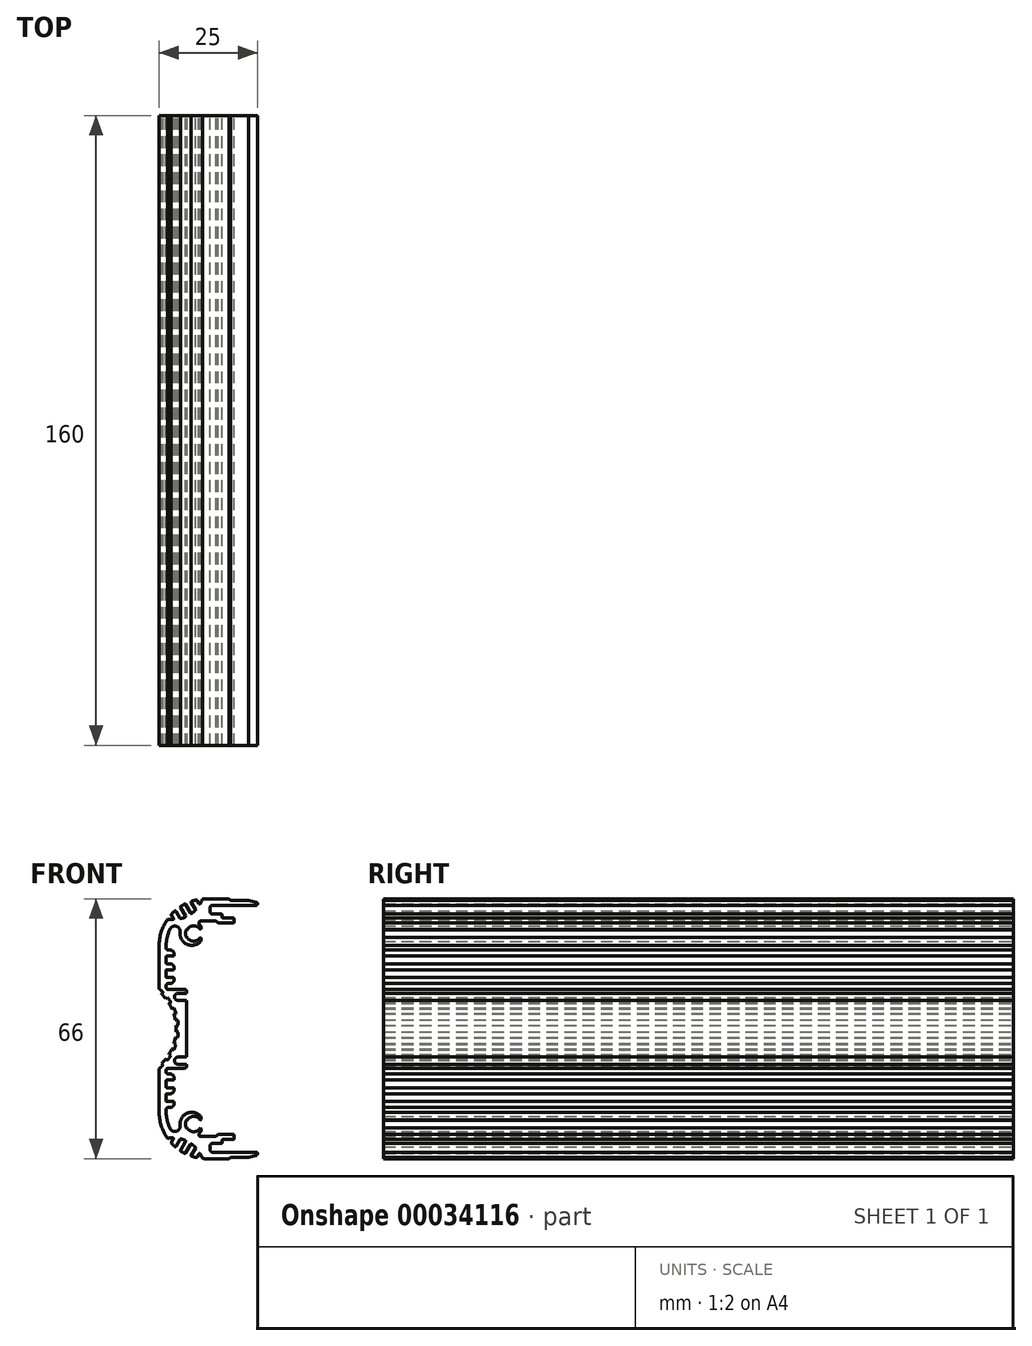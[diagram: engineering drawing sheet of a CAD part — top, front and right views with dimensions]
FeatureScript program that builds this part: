
annotation { "Feature Type Name" : "Feature", "Feature Type Description" : "" }
export const myFeature = defineFeature(function(context is Context, id is Id, definition is map)
    precondition{}
    {
        {
            var Q0;
            Q0=qCreatedBy(makeId("Front.planeOp"),FACE);
            var sketch = newSketch(context, id + "F0", { "sketchPlane" : qUnion([Q0])});
            skArc(sketch, "E0", {"start": v(-7.7, 9) * mm, "mid": v(-8.6, 8.1) * mm, "end": v(-7.7, 7.2) * mm});
            skLineSegment(sketch, "E1", {"start": v(-7.7, 9) * mm, "end": v(-5.5, 9) * mm});
            skLineSegment(sketch, "E2", {"start": v(-5.5, 9) * mm, "end": v(-5.5, 9.5) * mm});
            skArc(sketch, "E3", {"start": v(-5.5, 9.5) * mm, "mid": v(-5.65, 9.85) * mm, "end": v(-6, 10) * mm});
            skLineSegment(sketch, "E4", {"start": v(-6, 10) * mm, "end": v(-10.2, 10) * mm});
            skArc(sketch, "E5", {"start": v(-10.7, 10.5) * mm, "mid": v(-10.55, 10.15) * mm, "end": v(-10.2, 10) * mm});
            skLineSegment(sketch, "E6", {"start": v(-10.7, 10.5) * mm, "end": v(-10.7, 11) * mm});
            skArc(sketch, "E7", {"start": v(-10.2, 11.5) * mm, "mid": v(-10.55, 11.35) * mm, "end": v(-10.7, 11) * mm});
            skLineSegment(sketch, "E8", {"start": v(-10.2, 11.5) * mm, "end": v(-9.7, 11.5) * mm});
            skArc(sketch, "E9", {"start": v(-9.7, 11.5) * mm, "mid": v(-9, 11.8) * mm, "end": v(-8.7, 12.5) * mm});
            skLineSegment(sketch, "E10", {"start": v(-8.7, 12.5) * mm, "end": v(-8.7, 12.8) * mm});
            skArc(sketch, "E11", {"start": v(-8.7, 12.8) * mm, "mid": v(-8.76, 12.94) * mm, "end": v(-8.9, 13) * mm});
            skLineSegment(sketch, "E12", {"start": v(-8.9, 13) * mm, "end": v(-10.5, 13) * mm});
            skArc(sketch, "E13", {"start": v(-10.7, 13.2) * mm, "mid": v(-10.64, 13.06) * mm, "end": v(-10.5, 13) * mm});
            skLineSegment(sketch, "E14", {"start": v(-10.7, 13.2) * mm, "end": v(-10.7, 14.8) * mm});
            skArc(sketch, "E15", {"start": v(-10.5, 15) * mm, "mid": v(-10.64, 14.94) * mm, "end": v(-10.7, 14.8) * mm});
            skLineSegment(sketch, "E16", {"start": v(-10.5, 15) * mm, "end": v(-8.9, 15) * mm});
            skArc(sketch, "E17", {"start": v(-8.9, 15) * mm, "mid": v(-8.76, 15.06) * mm, "end": v(-8.7, 15.2) * mm});
            skLineSegment(sketch, "E18", {"start": v(-8.7, 15.2) * mm, "end": v(-8.7, 15.5) * mm});
            skArc(sketch, "E19", {"start": v(-8.7, 15.5) * mm, "mid": v(-9, 16.2) * mm, "end": v(-9.7, 16.5) * mm});
            skLineSegment(sketch, "E20", {"start": v(-9.7, 16.5) * mm, "end": v(-10.5, 16.5) * mm});
            skArc(sketch, "E21", {"start": v(-10.7, 16.7) * mm, "mid": v(-10.64, 16.56) * mm, "end": v(-10.5, 16.5) * mm});
            skLineSegment(sketch, "E22", {"start": v(-10.7, 16.7) * mm, "end": v(-10.7, 18.3) * mm});
            skArc(sketch, "E23", {"start": v(-10.5, 18.5) * mm, "mid": v(-10.64, 18.44) * mm, "end": v(-10.7, 18.3) * mm});
            skLineSegment(sketch, "E24", {"start": v(-10.5, 18.5) * mm, "end": v(-8.9, 18.5) * mm});
            skArc(sketch, "E25", {"start": v(-8.9, 18.5) * mm, "mid": v(-8.76, 18.56) * mm, "end": v(-8.7, 18.7) * mm});
            skLineSegment(sketch, "E26", {"start": v(-8.7, 18.7) * mm, "end": v(-8.7, 19) * mm});
            skArc(sketch, "E27", {"start": v(-8.7, 19) * mm, "mid": v(-9, 19.7) * mm, "end": v(-9.7, 20) * mm});
            skLineSegment(sketch, "E28", {"start": v(-9.7, 20) * mm, "end": v(-10.2, 20) * mm});
            skArc(sketch, "E29", {"start": v(-10.7, 20.5) * mm, "mid": v(-10.55, 20.15) * mm, "end": v(-10.2, 20) * mm});
            skLineSegment(sketch, "E30", {"start": v(-10.7, 20.5) * mm, "end": v(-10.7, 21) * mm});
            skArc(sketch, "E31", {"start": v(-9.74, 25.33) * mm, "mid": v(-10.46, 23.22) * mm, "end": v(-10.7, 21) * mm});
            skArc(sketch, "E32", {"start": v(-7.18, 24.58) * mm, "mid": v(-8.14, 26.05) * mm, "end": v(-9.74, 25.33) * mm});
            skArc(sketch, "E33", {"start": v(-7.18, 24.58) * mm, "mid": v(-5.47, 21.48) * mm, "end": v(-2, 22.16) * mm});
            skArc(sketch, "E34", {"start": v(-2, 22.16) * mm, "mid": v(-1.8, 22.69) * mm, "end": v(-2.02, 23.2) * mm});
            skArc(sketch, "E35", {"start": v(-5.39, 23.23) * mm, "mid": v(-3.71, 22.25) * mm, "end": v(-2.02, 23.2) * mm});
            skLineSegment(sketch, "E36", {"start": v(-5.39, 23.23) * mm, "end": v(-5.52, 23.15) * mm});
            skArc(sketch, "E37", {"start": v(-5.52, 25.25) * mm, "mid": v(-5.8, 24.2) * mm, "end": v(-5.52, 23.15) * mm});
            skLineSegment(sketch, "E38", {"start": v(-5.52, 25.25) * mm, "end": v(-5.39, 25.18) * mm});
            skArc(sketch, "E39", {"start": v(-2.02, 25.2) * mm, "mid": v(-3.71, 26.15) * mm, "end": v(-5.39, 25.17) * mm});
            skArc(sketch, "E40", {"start": v(-2.02, 25.2) * mm, "mid": v(-1.8, 25.71) * mm, "end": v(-2, 26.24) * mm});
            skArc(sketch, "E41", {"start": v(-2, 26.24) * mm, "mid": v(-2.12, 26.36) * mm, "end": v(-2.24, 26.47) * mm});
            skArc(sketch, "E42", {"start": v(-1.91, 27.35) * mm, "mid": v(-2.38, 27.02) * mm, "end": v(-2.24, 26.47) * mm});
            skLineSegment(sketch, "E43", {"start": v(-1.91, 27.35) * mm, "end": v(2, 27.35) * mm});
            skLineSegment(sketch, "E44", {"start": v(2, 27.35) * mm, "end": v(2.5, 26.85) * mm});
            skLineSegment(sketch, "E45", {"start": v(2.5, 26.85) * mm, "end": v(6.3, 26.85) * mm});
            skArc(sketch, "E46", {"start": v(6.3, 26.85) * mm, "mid": v(6.44, 26.9) * mm, "end": v(6.5, 27.05) * mm});
            skLineSegment(sketch, "E47", {"start": v(6.5, 27.05) * mm, "end": v(6.5, 27.95) * mm});
            skArc(sketch, "E48", {"start": v(6.5, 27.95) * mm, "mid": v(6.44, 28.1) * mm, "end": v(6.3, 28.15) * mm});
            skLineSegment(sketch, "E49", {"start": v(6.3, 28.15) * mm, "end": v(3.7, 28.15) * mm});
            skArc(sketch, "E50", {"start": v(3.5, 28.35) * mm, "mid": v(3.56, 28.2) * mm, "end": v(3.7, 28.15) * mm});
            skLineSegment(sketch, "E51", {"start": v(3.5, 28.35) * mm, "end": v(3.5, 28.95) * mm});
            skArc(sketch, "E52", {"start": v(3.5, 28.95) * mm, "mid": v(3.44, 29.1) * mm, "end": v(3.3, 29.15) * mm});
            skLineSegment(sketch, "E53", {"start": v(3.3, 29.15) * mm, "end": v(1, 29.15) * mm});
            skArc(sketch, "E54", {"start": v(0.5, 29.65) * mm, "mid": v(0.65, 29.3) * mm, "end": v(1, 29.15) * mm});
            skLineSegment(sketch, "E55", {"start": v(0.5, 29.65) * mm, "end": v(0.5, 30.85) * mm});
            skArc(sketch, "E56", {"start": v(1, 31.35) * mm, "mid": v(0.65, 31.2) * mm, "end": v(0.5, 30.85) * mm});
            skLineSegment(sketch, "E57", {"start": v(1, 31.35) * mm, "end": v(12.1, 31.35) * mm});
            skArc(sketch, "E58", {"start": v(12.1, 31.35) * mm, "mid": v(12.5, 31.7) * mm, "end": v(12.2, 32.14) * mm});
            skLineSegment(sketch, "E59", {"start": v(12.2, 32.14) * mm, "end": v(10.29, 32.65) * mm});
            skLineSegment(sketch, "E60", {"start": v(10.29, 32.65) * mm, "end": v(5.65, 32.65) * mm});
            skLineSegment(sketch, "E61", {"start": v(5.65, 32.65) * mm, "end": v(5.3, 33) * mm});
            skLineSegment(sketch, "E62", {"start": v(5.3, 33) * mm, "end": v(-0.5, 33) * mm});
            skArc(sketch, "E63", {"start": v(-0.5, 33) * mm, "mid": v(-1, 32.99) * mm, "end": v(-1.5, 32.96) * mm});
            skArc(sketch, "E64", {"start": v(-2.04, 31.77) * mm, "mid": v(-1.74, 32.36) * mm, "end": v(-1.5, 32.96) * mm});
            skArc(sketch, "E65", {"start": v(-2.39, 31.77) * mm, "mid": v(-2.21, 31.67) * mm, "end": v(-2.04, 31.77) * mm});
            skLineSegment(sketch, "E66", {"start": v(-2.39, 31.77) * mm, "end": v(-2.88, 32.62) * mm});
            skArc(sketch, "E67", {"start": v(-2.88, 32.62) * mm, "mid": v(-2.97, 32.7) * mm, "end": v(-3.1, 32.72) * mm});
            skArc(sketch, "E68", {"start": v(-3.1, 32.72) * mm, "mid": v(-3.66, 32.58) * mm, "end": v(-4.21, 32.41) * mm});
            skArc(sketch, "E69", {"start": v(-4.21, 32.41) * mm, "mid": v(-4.34, 32.3) * mm, "end": v(-4.32, 32.12) * mm});
            skLineSegment(sketch, "E70", {"start": v(-4.32, 32.12) * mm, "end": v(-3.29, 30.33) * mm});
            skArc(sketch, "E71", {"start": v(-3.32, 30.09) * mm, "mid": v(-3.26, 30.2) * mm, "end": v(-3.29, 30.33) * mm});
            skArc(sketch, "E72", {"start": v(-4.18, 29.33) * mm, "mid": v(-3.74, 29.7) * mm, "end": v(-3.32, 30.09) * mm});
            skArc(sketch, "E73", {"start": v(-4.48, 29.4) * mm, "mid": v(-4.34, 29.3) * mm, "end": v(-4.18, 29.33) * mm});
            skLineSegment(sketch, "E74", {"start": v(-4.48, 29.4) * mm, "end": v(-5.74, 31.58) * mm});
            skArc(sketch, "E75", {"start": v(-5.74, 31.58) * mm, "mid": v(-5.86, 31.68) * mm, "end": v(-6, 31.66) * mm});
            skArc(sketch, "E76", {"start": v(-6, 31.66) * mm, "mid": v(-6.5, 31.4) * mm, "end": v(-6.98, 31.1) * mm});
            skArc(sketch, "E77", {"start": v(-6.98, 31.1) * mm, "mid": v(-7.07, 30.98) * mm, "end": v(-7.04, 30.83) * mm});
            skLineSegment(sketch, "E78", {"start": v(-7.04, 30.83) * mm, "end": v(-5.78, 28.64) * mm});
            skArc(sketch, "E79", {"start": v(-5.87, 28.36) * mm, "mid": v(-5.76, 28.48) * mm, "end": v(-5.78, 28.64) * mm});
            skArc(sketch, "E80", {"start": v(-6.96, 27.98) * mm, "mid": v(-6.41, 28.15) * mm, "end": v(-5.87, 28.36) * mm});
            skArc(sketch, "E81", {"start": v(-7.19, 28.08) * mm, "mid": v(-7.09, 28) * mm, "end": v(-6.96, 27.98) * mm});
            skLineSegment(sketch, "E82", {"start": v(-7.19, 28.08) * mm, "end": v(-8.22, 29.87) * mm});
            skArc(sketch, "E83", {"start": v(-8.22, 29.87) * mm, "mid": v(-8.36, 29.97) * mm, "end": v(-8.53, 29.92) * mm});
            skArc(sketch, "E84", {"start": v(-8.53, 29.92) * mm, "mid": v(-8.95, 29.52) * mm, "end": v(-9.35, 29.1) * mm});
            skArc(sketch, "E85", {"start": v(-9.35, 29.1) * mm, "mid": v(-9.4, 29) * mm, "end": v(-9.38, 28.87) * mm});
            skLineSegment(sketch, "E86", {"start": v(-9.38, 28.87) * mm, "end": v(-8.88, 28.02) * mm});
            skArc(sketch, "E87", {"start": v(-9.06, 27.72) * mm, "mid": v(-8.89, 27.82) * mm, "end": v(-8.88, 28.02) * mm});
            skArc(sketch, "E88", {"start": v(-10.36, 27.84) * mm, "mid": v(-9.71, 27.75) * mm, "end": v(-9.06, 27.72) * mm});
            skArc(sketch, "E89", {"start": v(-10.36, 27.84) * mm, "mid": v(-11.95, 24.58) * mm, "end": v(-12.5, 21) * mm});
            skLineSegment(sketch, "E90", {"start": v(-12.5, 21) * mm, "end": v(-12.5, 10.13) * mm});
            skArc(sketch, "E91", {"start": v(-11.49, 9.24) * mm, "mid": v(-11.98, 9.7) * mm, "end": v(-12.5, 10.13) * mm});
            skLineSegment(sketch, "E92", {"start": v(-11.49, 9.24) * mm, "end": v(-11.9, 8.83) * mm});
            skArc(sketch, "E93", {"start": v(-10.82, 7.64) * mm, "mid": v(-11.34, 8.25) * mm, "end": v(-11.9, 8.83) * mm});
            skLineSegment(sketch, "E94", {"start": v(-10.82, 7.64) * mm, "end": v(-10.37, 8) * mm});
            skArc(sketch, "E95", {"start": v(-9.52, 6.79) * mm, "mid": v(-9.92, 7.4) * mm, "end": v(-10.37, 8) * mm});
            skLineSegment(sketch, "E96", {"start": v(-9.52, 6.79) * mm, "end": v(-10.01, 6.48) * mm});
            skArc(sketch, "E97", {"start": v(-9.26, 5.07) * mm, "mid": v(-9.61, 5.79) * mm, "end": v(-10.01, 6.48) * mm});
            skLineSegment(sketch, "E98", {"start": v(-9.26, 5.07) * mm, "end": v(-8.73, 5.3) * mm});
            skArc(sketch, "E99", {"start": v(-8.2, 3.93) * mm, "mid": v(-8.45, 4.63) * mm, "end": v(-8.73, 5.3) * mm});
            skLineSegment(sketch, "E100", {"start": v(-8.2, 3.93) * mm, "end": v(-8.76, 3.75) * mm});
            skArc(sketch, "E101", {"start": v(-8.37, 2.2) * mm, "mid": v(-8.54, 2.98) * mm, "end": v(-8.75, 3.75) * mm});
            skLineSegment(sketch, "E102", {"start": v(-8.37, 2.2) * mm, "end": v(-7.8, 2.3) * mm});
            skArc(sketch, "E103", {"start": v(-7.62, 0.84) * mm, "mid": v(-7.69, 1.57) * mm, "end": v(-7.8, 2.3) * mm});
            skLineSegment(sketch, "E104", {"start": v(-7.62, 0.84) * mm, "end": v(-8.2, 0.8) * mm});
            skArc(sketch, "E105", {"start": v(-8.2, -0.8) * mm, "mid": v(-8.17, 0) * mm, "end": v(-8.2, 0.8) * mm});
            skLineSegment(sketch, "E106", {"start": v(-8.2, -0.8) * mm, "end": v(-7.62, -0.84) * mm});
            skArc(sketch, "E107", {"start": v(-7.8, -2.3) * mm, "mid": v(-7.69, -1.57) * mm, "end": v(-7.62, -0.84) * mm});
            skLineSegment(sketch, "E108", {"start": v(-7.8, -2.3) * mm, "end": v(-8.37, -2.2) * mm});
            skArc(sketch, "E109", {"start": v(-8.75, -3.75) * mm, "mid": v(-8.54, -2.98) * mm, "end": v(-8.37, -2.2) * mm});
            skLineSegment(sketch, "E110", {"start": v(-8.76, -3.75) * mm, "end": v(-8.2, -3.93) * mm});
            skArc(sketch, "E111", {"start": v(-8.73, -5.3) * mm, "mid": v(-8.45, -4.63) * mm, "end": v(-8.2, -3.93) * mm});
            skLineSegment(sketch, "E112", {"start": v(-8.73, -5.3) * mm, "end": v(-9.26, -5.07) * mm});
            skArc(sketch, "E113", {"start": v(-10.01, -6.48) * mm, "mid": v(-9.61, -5.79) * mm, "end": v(-9.26, -5.07) * mm});
            skLineSegment(sketch, "E114", {"start": v(-10.01, -6.48) * mm, "end": v(-9.52, -6.79) * mm});
            skArc(sketch, "E115", {"start": v(-10.37, -8) * mm, "mid": v(-9.92, -7.4) * mm, "end": v(-9.52, -6.79) * mm});
            skLineSegment(sketch, "E116", {"start": v(-10.37, -8) * mm, "end": v(-10.82, -7.64) * mm});
            skArc(sketch, "E117", {"start": v(-11.9, -8.83) * mm, "mid": v(-11.34, -8.25) * mm, "end": v(-10.82, -7.64) * mm});
            skLineSegment(sketch, "E118", {"start": v(-11.9, -8.83) * mm, "end": v(-11.49, -9.24) * mm});
            skArc(sketch, "E119", {"start": v(-12.5, -10.13) * mm, "mid": v(-11.98, -9.7) * mm, "end": v(-11.49, -9.24) * mm});
            skLineSegment(sketch, "E120", {"start": v(-12.5, -10.13) * mm, "end": v(-12.5, -21) * mm});
            skArc(sketch, "E121", {"start": v(-12.5, -21) * mm, "mid": v(-11.95, -24.58) * mm, "end": v(-10.36, -27.84) * mm});
            skArc(sketch, "E122", {"start": v(-9.06, -27.72) * mm, "mid": v(-9.71, -27.75) * mm, "end": v(-10.36, -27.84) * mm});
            skArc(sketch, "E123", {"start": v(-8.88, -28.02) * mm, "mid": v(-8.89, -27.82) * mm, "end": v(-9.06, -27.72) * mm});
            skLineSegment(sketch, "E124", {"start": v(-8.88, -28.02) * mm, "end": v(-9.38, -28.87) * mm});
            skArc(sketch, "E125", {"start": v(-9.38, -28.87) * mm, "mid": v(-9.4, -29) * mm, "end": v(-9.35, -29.1) * mm});
            skArc(sketch, "E126", {"start": v(-9.35, -29.1) * mm, "mid": v(-8.95, -29.52) * mm, "end": v(-8.53, -29.92) * mm});
            skArc(sketch, "E127", {"start": v(-8.53, -29.92) * mm, "mid": v(-8.36, -29.97) * mm, "end": v(-8.22, -29.87) * mm});
            skLineSegment(sketch, "E128", {"start": v(-8.22, -29.87) * mm, "end": v(-7.19, -28.08) * mm});
            skArc(sketch, "E129", {"start": v(-6.96, -27.98) * mm, "mid": v(-7.09, -28) * mm, "end": v(-7.19, -28.08) * mm});
            skArc(sketch, "E130", {"start": v(-5.87, -28.36) * mm, "mid": v(-6.41, -28.15) * mm, "end": v(-6.96, -27.98) * mm});
            skArc(sketch, "E131", {"start": v(-5.78, -28.64) * mm, "mid": v(-5.76, -28.48) * mm, "end": v(-5.87, -28.36) * mm});
            skLineSegment(sketch, "E132", {"start": v(-5.78, -28.64) * mm, "end": v(-7.04, -30.83) * mm});
            skArc(sketch, "E133", {"start": v(-7.04, -30.83) * mm, "mid": v(-7.07, -30.98) * mm, "end": v(-6.98, -31.1) * mm});
            skArc(sketch, "E134", {"start": v(-6.98, -31.1) * mm, "mid": v(-6.5, -31.4) * mm, "end": v(-6, -31.66) * mm});
            skArc(sketch, "E135", {"start": v(-6, -31.66) * mm, "mid": v(-5.86, -31.68) * mm, "end": v(-5.74, -31.58) * mm});
            skLineSegment(sketch, "E136", {"start": v(-5.74, -31.58) * mm, "end": v(-4.48, -29.4) * mm});
            skArc(sketch, "E137", {"start": v(-4.18, -29.33) * mm, "mid": v(-4.34, -29.3) * mm, "end": v(-4.48, -29.4) * mm});
            skArc(sketch, "E138", {"start": v(-3.32, -30.09) * mm, "mid": v(-3.74, -29.7) * mm, "end": v(-4.18, -29.33) * mm});
            skArc(sketch, "E139", {"start": v(-3.29, -30.33) * mm, "mid": v(-3.26, -30.2) * mm, "end": v(-3.32, -30.09) * mm});
            skLineSegment(sketch, "E140", {"start": v(-3.29, -30.33) * mm, "end": v(-4.32, -32.12) * mm});
            skArc(sketch, "E141", {"start": v(-4.32, -32.12) * mm, "mid": v(-4.34, -32.3) * mm, "end": v(-4.21, -32.41) * mm});
            skArc(sketch, "E142", {"start": v(-4.21, -32.41) * mm, "mid": v(-3.66, -32.58) * mm, "end": v(-3.1, -32.72) * mm});
            skArc(sketch, "E143", {"start": v(-3.1, -32.72) * mm, "mid": v(-2.97, -32.7) * mm, "end": v(-2.88, -32.62) * mm});
            skLineSegment(sketch, "E144", {"start": v(-2.88, -32.62) * mm, "end": v(-2.39, -31.77) * mm});
            skArc(sketch, "E145", {"start": v(-2.04, -31.77) * mm, "mid": v(-2.21, -31.67) * mm, "end": v(-2.39, -31.77) * mm});
            skArc(sketch, "E146", {"start": v(-1.5, -32.96) * mm, "mid": v(-1.74, -32.36) * mm, "end": v(-2.04, -31.77) * mm});
            skArc(sketch, "E147", {"start": v(-1.5, -32.96) * mm, "mid": v(-1, -32.99) * mm, "end": v(-0.5, -33) * mm});
            skLineSegment(sketch, "E148", {"start": v(-0.5, -33) * mm, "end": v(5.3, -33) * mm});
            skLineSegment(sketch, "E149", {"start": v(5.3, -33) * mm, "end": v(5.65, -32.65) * mm});
            skLineSegment(sketch, "E150", {"start": v(5.65, -32.65) * mm, "end": v(10.29, -32.65) * mm});
            skLineSegment(sketch, "E151", {"start": v(10.29, -32.65) * mm, "end": v(12.2, -32.14) * mm});
            skArc(sketch, "E152", {"start": v(12.2, -32.14) * mm, "mid": v(12.5, -31.7) * mm, "end": v(12.1, -31.35) * mm});
            skLineSegment(sketch, "E153", {"start": v(12.1, -31.35) * mm, "end": v(1, -31.35) * mm});
            skArc(sketch, "E154", {"start": v(0.5, -30.85) * mm, "mid": v(0.65, -31.2) * mm, "end": v(1, -31.35) * mm});
            skLineSegment(sketch, "E155", {"start": v(0.5, -30.85) * mm, "end": v(0.5, -29.65) * mm});
            skArc(sketch, "E156", {"start": v(1, -29.15) * mm, "mid": v(0.65, -29.3) * mm, "end": v(0.5, -29.65) * mm});
            skLineSegment(sketch, "E157", {"start": v(1, -29.15) * mm, "end": v(3.3, -29.15) * mm});
            skArc(sketch, "E158", {"start": v(3.3, -29.15) * mm, "mid": v(3.44, -29.1) * mm, "end": v(3.5, -28.95) * mm});
            skLineSegment(sketch, "E159", {"start": v(3.5, -28.95) * mm, "end": v(3.5, -28.35) * mm});
            skArc(sketch, "E160", {"start": v(3.7, -28.15) * mm, "mid": v(3.56, -28.2) * mm, "end": v(3.5, -28.35) * mm});
            skLineSegment(sketch, "E161", {"start": v(3.7, -28.15) * mm, "end": v(6.3, -28.15) * mm});
            skArc(sketch, "E162", {"start": v(6.3, -28.15) * mm, "mid": v(6.44, -28.1) * mm, "end": v(6.5, -27.95) * mm});
            skLineSegment(sketch, "E163", {"start": v(6.5, -27.95) * mm, "end": v(6.5, -27.05) * mm});
            skArc(sketch, "E164", {"start": v(6.5, -27.05) * mm, "mid": v(6.44, -26.9) * mm, "end": v(6.3, -26.85) * mm});
            skLineSegment(sketch, "E165", {"start": v(6.3, -26.85) * mm, "end": v(2.5, -26.85) * mm});
            skLineSegment(sketch, "E166", {"start": v(2.5, -26.85) * mm, "end": v(2, -27.35) * mm});
            skLineSegment(sketch, "E167", {"start": v(2, -27.35) * mm, "end": v(-1.91, -27.35) * mm});
            skArc(sketch, "E168", {"start": v(-2.24, -26.47) * mm, "mid": v(-2.38, -27.02) * mm, "end": v(-1.91, -27.35) * mm});
            skArc(sketch, "E169", {"start": v(-2.24, -26.47) * mm, "mid": v(-2.12, -26.36) * mm, "end": v(-2, -26.24) * mm});
            skArc(sketch, "E170", {"start": v(-2, -26.24) * mm, "mid": v(-1.8, -25.71) * mm, "end": v(-2.02, -25.2) * mm});
            skArc(sketch, "E171", {"start": v(-5.39, -25.17) * mm, "mid": v(-3.71, -26.15) * mm, "end": v(-2.02, -25.2) * mm});
            skLineSegment(sketch, "E172", {"start": v(-5.39, -25.18) * mm, "end": v(-5.52, -25.25) * mm});
            skArc(sketch, "E173", {"start": v(-5.52, -23.15) * mm, "mid": v(-5.8, -24.2) * mm, "end": v(-5.52, -25.25) * mm});
            skLineSegment(sketch, "E174", {"start": v(-5.52, -23.15) * mm, "end": v(-5.39, -23.23) * mm});
            skArc(sketch, "E175", {"start": v(-2.02, -23.2) * mm, "mid": v(-3.71, -22.25) * mm, "end": v(-5.39, -23.23) * mm});
            skArc(sketch, "E176", {"start": v(-2.02, -23.2) * mm, "mid": v(-1.8, -22.69) * mm, "end": v(-2, -22.16) * mm});
            skArc(sketch, "E177", {"start": v(-2, -22.16) * mm, "mid": v(-5.47, -21.48) * mm, "end": v(-7.18, -24.58) * mm});
            skArc(sketch, "E178", {"start": v(-9.74, -25.33) * mm, "mid": v(-8.14, -26.05) * mm, "end": v(-7.18, -24.58) * mm});
            skArc(sketch, "E179", {"start": v(-10.7, -21) * mm, "mid": v(-10.46, -23.22) * mm, "end": v(-9.74, -25.33) * mm});
            skLineSegment(sketch, "E180", {"start": v(-10.7, -21) * mm, "end": v(-10.7, -20.5) * mm});
            skArc(sketch, "E181", {"start": v(-10.2, -20) * mm, "mid": v(-10.55, -20.15) * mm, "end": v(-10.7, -20.5) * mm});
            skLineSegment(sketch, "E182", {"start": v(-10.2, -20) * mm, "end": v(-9.7, -20) * mm});
            skArc(sketch, "E183", {"start": v(-9.7, -20) * mm, "mid": v(-9, -19.7) * mm, "end": v(-8.7, -19) * mm});
            skLineSegment(sketch, "E184", {"start": v(-8.7, -19) * mm, "end": v(-8.7, -18.7) * mm});
            skArc(sketch, "E185", {"start": v(-8.7, -18.7) * mm, "mid": v(-8.76, -18.56) * mm, "end": v(-8.9, -18.5) * mm});
            skLineSegment(sketch, "E186", {"start": v(-8.9, -18.5) * mm, "end": v(-10.5, -18.5) * mm});
            skArc(sketch, "E187", {"start": v(-10.7, -18.3) * mm, "mid": v(-10.64, -18.44) * mm, "end": v(-10.5, -18.5) * mm});
            skLineSegment(sketch, "E188", {"start": v(-10.7, -18.3) * mm, "end": v(-10.7, -16.7) * mm});
            skArc(sketch, "E189", {"start": v(-10.5, -16.5) * mm, "mid": v(-10.64, -16.56) * mm, "end": v(-10.7, -16.7) * mm});
            skLineSegment(sketch, "E190", {"start": v(-10.5, -16.5) * mm, "end": v(-9.7, -16.5) * mm});
            skArc(sketch, "E191", {"start": v(-9.7, -16.5) * mm, "mid": v(-9, -16.2) * mm, "end": v(-8.7, -15.5) * mm});
            skLineSegment(sketch, "E192", {"start": v(-8.7, -15.5) * mm, "end": v(-8.7, -15.2) * mm});
            skArc(sketch, "E193", {"start": v(-8.7, -15.2) * mm, "mid": v(-8.76, -15.06) * mm, "end": v(-8.9, -15) * mm});
            skLineSegment(sketch, "E194", {"start": v(-8.9, -15) * mm, "end": v(-10.5, -15) * mm});
            skArc(sketch, "E195", {"start": v(-10.7, -14.8) * mm, "mid": v(-10.64, -14.94) * mm, "end": v(-10.5, -15) * mm});
            skLineSegment(sketch, "E196", {"start": v(-10.7, -14.8) * mm, "end": v(-10.7, -13.2) * mm});
            skArc(sketch, "E197", {"start": v(-10.5, -13) * mm, "mid": v(-10.64, -13.06) * mm, "end": v(-10.7, -13.2) * mm});
            skLineSegment(sketch, "E198", {"start": v(-10.5, -13) * mm, "end": v(-8.9, -13) * mm});
            skArc(sketch, "E199", {"start": v(-8.9, -13) * mm, "mid": v(-8.76, -12.94) * mm, "end": v(-8.7, -12.8) * mm});
            skLineSegment(sketch, "E200", {"start": v(-8.7, -12.8) * mm, "end": v(-8.7, -12.5) * mm});
            skArc(sketch, "E201", {"start": v(-8.7, -12.5) * mm, "mid": v(-9, -11.8) * mm, "end": v(-9.7, -11.5) * mm});
            skLineSegment(sketch, "E202", {"start": v(-9.7, -11.5) * mm, "end": v(-10.2, -11.5) * mm});
            skArc(sketch, "E203", {"start": v(-10.7, -11) * mm, "mid": v(-10.55, -11.35) * mm, "end": v(-10.2, -11.5) * mm});
            skLineSegment(sketch, "E204", {"start": v(-10.7, -11) * mm, "end": v(-10.7, -10.5) * mm});
            skArc(sketch, "E205", {"start": v(-10.2, -10) * mm, "mid": v(-10.55, -10.15) * mm, "end": v(-10.7, -10.5) * mm});
            skLineSegment(sketch, "E206", {"start": v(-10.2, -10) * mm, "end": v(-6, -10) * mm});
            skArc(sketch, "E207", {"start": v(-6, -10) * mm, "mid": v(-5.65, -9.85) * mm, "end": v(-5.5, -9.5) * mm});
            skLineSegment(sketch, "E208", {"start": v(-5.5, -9.5) * mm, "end": v(-5.5, -9) * mm});
            skLineSegment(sketch, "E209", {"start": v(-5.5, -9) * mm, "end": v(-7.7, -9) * mm});
            skArc(sketch, "E210", {"start": v(-7.7, -7.2) * mm, "mid": v(-8.6, -8.1) * mm, "end": v(-7.7, -9) * mm});
            skLineSegment(sketch, "E211", {"start": v(-7.7, -7.2) * mm, "end": v(-5.5, -7.2) * mm});
            skLineSegment(sketch, "E212", {"start": v(-5.5, -7.2) * mm, "end": v(-5.5, 7.2) * mm});
            skLineSegment(sketch, "E213", {"start": v(-5.5, 7.2) * mm, "end": v(-7.7, 7.2) * mm});
            skSolve(sketch);
        }
        {
            var Q0;
            Q0=qSketchRegion(id+"F0",true);
            extrude(context, id + "F1", {"entities" : qUnion([Q0]), "depth" : 160 * mm});
        }
    });
